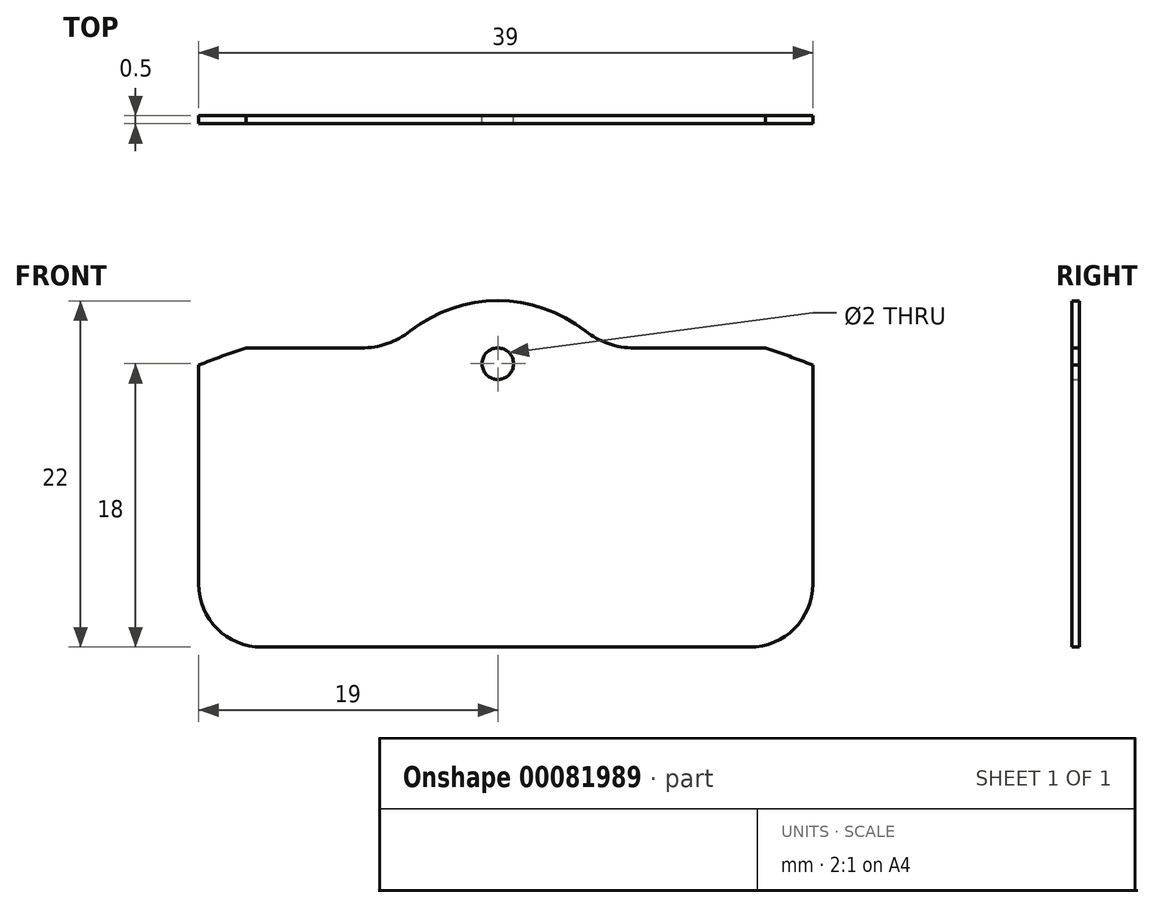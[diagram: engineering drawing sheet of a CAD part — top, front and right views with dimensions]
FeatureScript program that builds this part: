
annotation { "Feature Type Name" : "Feature", "Feature Type Description" : "" }
export const myFeature = defineFeature(function(context is Context, id is Id, definition is map)
    precondition{}
    {
        {
            var Q0;
            Q0=qCreatedBy(makeId("Front.planeOp"),FACE);
            var sketch = newSketch(context, id + "F0", { "sketchPlane" : qUnion([Q0])});
            skLineSegment(sketch, "E0.bottom", {"start": v(4, 0) * mm, "end": v(35, 0) * mm});
            skLineSegment(sketch, "E0.top", {"start": v(3, 19) * mm, "end": v(10.34, 19) * mm});
            skLineSegment(sketch, "E0.left", {"start": v(0, 4) * mm, "end": v(0, 17.9) * mm});
            skLineSegment(sketch, "E0.right", {"start": v(39, 4) * mm, "end": v(39, 17.9) * mm});
            skCircle(sketch, "E1", {"center": v(19, 18) * mm, "radius": 1 * mm});
            skArc(sketch, "E2", {"start": v(24.57, 20.07) * mm, "mid": v(19, 22) * mm, "end": v(13.43, 20.07) * mm});
            skLineSegment(sketch, "E3.trimOffspring", {"start": v(27.66, 19) * mm, "end": v(36, 19) * mm});
            skPoint(sketch, "E4.visualSharp", {"position": v(12.3, 19) * mm});
            skArc(sketch, "E4.filletArc", {"start": v(10.34, 19) * mm, "mid": v(11.98, 19.28) * mm, "end": v(13.43, 20.07) * mm});
            skPoint(sketch, "E5.visualSharp", {"position": v(25.7, 19) * mm});
            skArc(sketch, "E5.filletArc", {"start": v(24.57, 20.07) * mm, "mid": v(26.02, 19.28) * mm, "end": v(27.66, 19) * mm});
            skPoint(sketch, "E6.visualSharp", {"position": v(0, 0) * mm});
            skArc(sketch, "E6.filletArc", {"start": v(0, 4) * mm, "mid": v(1.17, 1.17) * mm, "end": v(4, 0) * mm});
            skPoint(sketch, "E7.visualSharp", {"position": v(39, 0) * mm});
            skArc(sketch, "E7.filletArc", {"start": v(35, 0) * mm, "mid": v(37.83, 1.17) * mm, "end": v(39, 4) * mm});
            skArc(sketch, "E8", {"start": v(3, 19) * mm, "mid": v(1.5, 18.48) * mm, "end": v(0, 17.9) * mm});
            skArc(sketch, "E9.trimOffspring", {"start": v(39, 17.9) * mm, "mid": v(37.5, 18.48) * mm, "end": v(36, 19) * mm});
            skSolve(sketch);
        }
        {
            var Q0;
            Q0=makeQuery(id+"F0.imprint","IMPRINT",FACE,{"disambiguationData":[TD([[makeQuery(id+"F0.imprint","IMPRINT",EDGE,{"derivedFrom":sQuery(id+"F0.wireOp",EDGE,"E0.bottom")}),1.0]])]});
            extrude(context, id + "F1", {"entities" : qUnion([Q0]), "depth" : 0.5 * mm});
        }
    });
